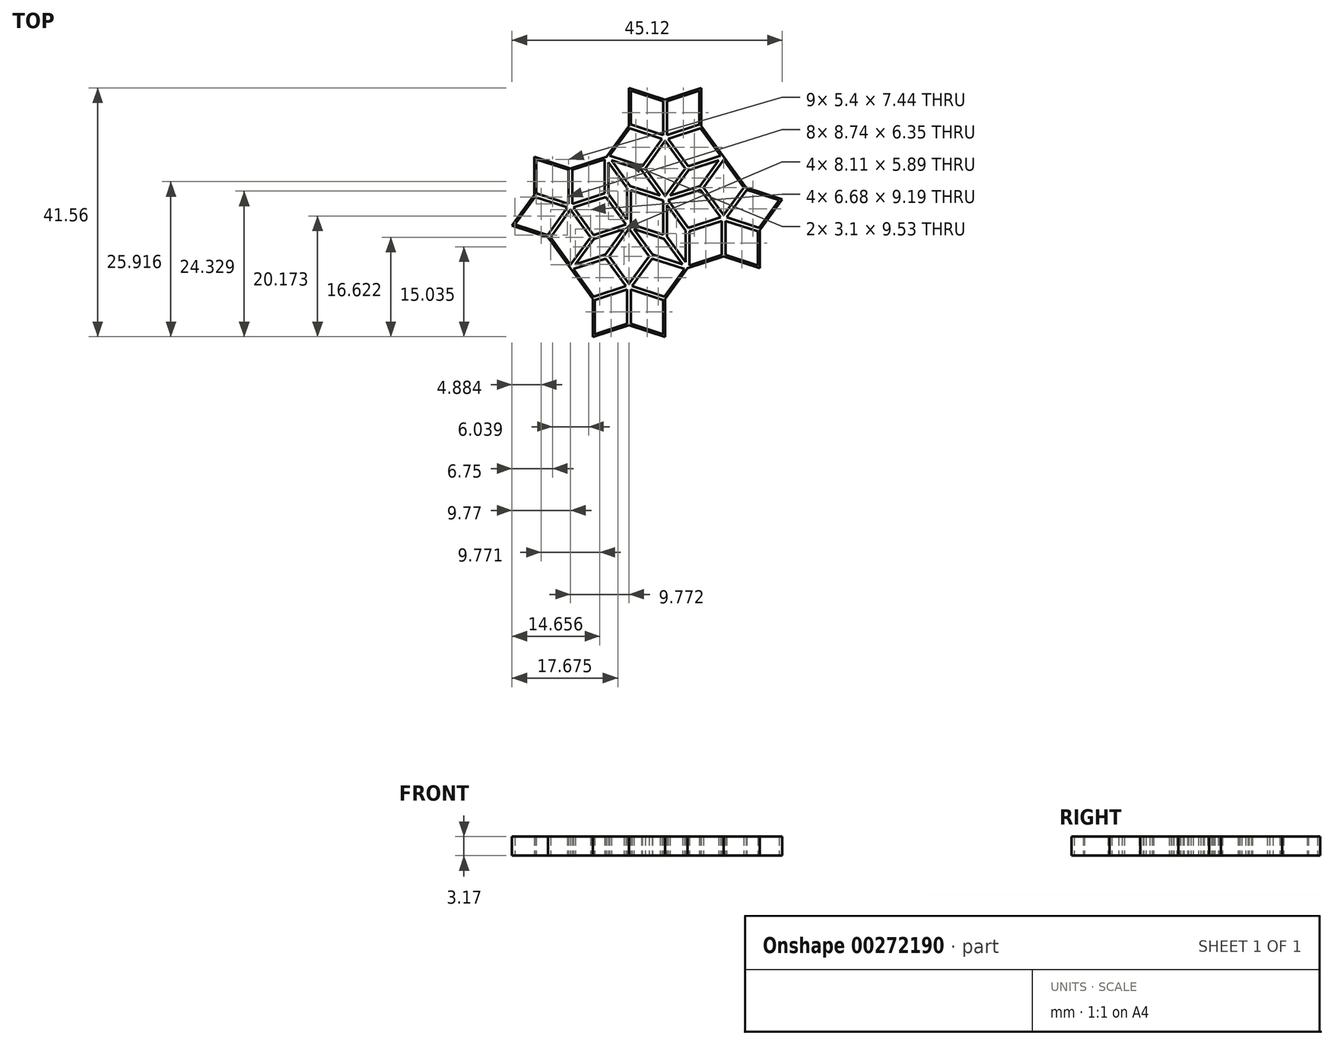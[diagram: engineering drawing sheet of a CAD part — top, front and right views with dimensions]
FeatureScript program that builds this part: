
annotation { "Feature Type Name" : "Feature", "Feature Type Description" : "" }
export const myFeature = defineFeature(function(context is Context, id is Id, definition is map)
    precondition{}
    {
        {
            var Q0;
            Q0=qCreatedBy(makeId("Top.planeOp"),FACE);
            var sketch = newSketch(context, id + "F0", { "sketchPlane" : qUnion([Q0])});
            skLineSegment(sketch, "E0", {"start": v(0, 0) * mm, "end": v(0, 6.35) * mm, "construction": true});
            skLineSegment(sketch, "E1", {"start": v(0, 6.35) * mm, "end": v(-6.04, 8.31) * mm});
            skLineSegment(sketch, "E2", {"start": v(-6.04, 8.31) * mm, "end": v(-6.04, 1.96) * mm});
            skLineSegment(sketch, "E3", {"start": v(0, 0) * mm, "end": v(-6.04, 1.96) * mm, "construction": true});
            skLineSegment(sketch, "E4.1.0", {"start": v(-6.04, 1.96) * mm, "end": v(-9.77, -3.18) * mm});
            skLineSegment(sketch, "E4.1.2", {"start": v(0, 0) * mm, "end": v(-3.73, -5.14) * mm, "construction": true});
            skLineSegment(sketch, "E4.1.3", {"start": v(-9.77, -3.17) * mm, "end": v(-3.73, -5.14) * mm});
            skLineSegment(sketch, "E4.2.0", {"start": v(-3.73, -5.14) * mm, "end": v(0, -10.27) * mm});
            skLineSegment(sketch, "E4.2.3", {"start": v(0, -10.27) * mm, "end": v(3.73, -5.14) * mm, "construction": true});
            skLineSegment(sketch, "E4.3.0", {"start": v(3.73, -5.14) * mm, "end": v(10.09, -3.07) * mm, "construction": true});
            skLineSegment(sketch, "E4.4.0", {"start": v(6.04, 1.96) * mm, "end": v(6.04, 8.31) * mm, "construction": true});
            skLineSegment(sketch, "E4.4.3", {"start": v(6.04, 8.31) * mm, "end": v(0, 6.35) * mm});
            skPoint(sketch, "E4.center", {"position": v(0, 0) * mm});
            skLineSegment(sketch, "E5", {"start": v(5.72, 2.2) * mm, "end": v(0.32, 0.44) * mm});
            skLineSegment(sketch, "E6", {"start": v(0.32, 0.43) * mm, "end": v(0.32, 6.12) * mm});
            skLineSegment(sketch, "E7.1.2", {"start": v(-0.32, 6.12) * mm, "end": v(-0.32, 0.44) * mm});
            skLineSegment(sketch, "E7.1.3", {"start": v(-0.32, 0.44) * mm, "end": v(-5.72, 2.2) * mm});
            skLineSegment(sketch, "E7.2.2", {"start": v(-5.92, 1.59) * mm, "end": v(-0.51, -0.17) * mm});
            skLineSegment(sketch, "E7.2.3", {"start": v(-0.51, -0.17) * mm, "end": v(-3.85, -4.76) * mm});
            skLineSegment(sketch, "E7.4.2", {"start": v(3.85, -4.76) * mm, "end": v(0.51, -0.17) * mm});
            skLineSegment(sketch, "E8", {"start": v(0, 0) * mm, "end": v(3.73, -5.14) * mm, "construction": true});
            skLineSegment(sketch, "E9", {"start": v(0.32, 6.12) * mm, "end": v(5.72, 7.88) * mm});
            skLineSegment(sketch, "E10", {"start": v(5.72, 7.88) * mm, "end": v(5.72, 2.2) * mm});
            skLineSegment(sketch, "E11.1.0", {"start": v(-5.72, 2.2) * mm, "end": v(-5.72, 7.88) * mm});
            skLineSegment(sketch, "E11.1.1", {"start": v(-5.72, 7.88) * mm, "end": v(-0.32, 6.12) * mm});
            skLineSegment(sketch, "E11.2.0", {"start": v(-3.85, -4.76) * mm, "end": v(-9.26, -3) * mm});
            skLineSegment(sketch, "E11.2.1", {"start": v(-9.26, -3) * mm, "end": v(-5.92, 1.59) * mm});
            skLineSegment(sketch, "E11.4.0", {"start": v(5.92, 1.59) * mm, "end": v(9.26, -3) * mm});
            skLineSegment(sketch, "E11.4.1", {"start": v(9.26, -3) * mm, "end": v(3.85, -4.76) * mm});
            skLineSegment(sketch, "E12", {"start": v(0, 0) * mm, "end": v(6.04, 1.96) * mm, "construction": true});
            skLineSegment(sketch, "E13", {"start": v(0.51, -0.17) * mm, "end": v(5.92, 1.59) * mm});
            skLineSegment(sketch, "E14.MirrorCS", {"start": v(3.34, -5.14) * mm, "end": v(0, -0.54) * mm});
            skLineSegment(sketch, "E15.MirrorCS", {"start": v(0, -0.54) * mm, "end": v(-3.34, -5.14) * mm});
            skLineSegment(sketch, "E16.MirrorCS", {"start": v(-3.34, -5.14) * mm, "end": v(0, -9.73) * mm});
            skLineSegment(sketch, "E17.MirrorCS", {"start": v(0, -9.73) * mm, "end": v(3.34, -5.14) * mm});
            skLineSegment(sketch, "E18", {"start": v(6.04, 8.31) * mm, "end": v(9.76, -3.14) * mm, "construction": true});
            skLineSegment(sketch, "E19.MirrorCS", {"start": v(9.77, 3.17) * mm, "end": v(6.04, 8.31) * mm, "construction": true});
            skLineSegment(sketch, "E20.MirrorCS", {"start": v(9.77, -3.05) * mm, "end": v(9.77, 3.18) * mm, "construction": true});
            skLineSegment(sketch, "E21.MirrorCS", {"start": v(9.77, -3.18) * mm, "end": v(6.04, 1.96) * mm, "construction": true});
            skLineSegment(sketch, "E22.MirrorCS", {"start": v(15.81, 5.14) * mm, "end": v(9.77, 3.18) * mm, "construction": true});
            skLineSegment(sketch, "E23.MirrorCS", {"start": v(6.36, 7.34) * mm, "end": v(9.45, 3.07) * mm});
            skLineSegment(sketch, "E24.MirrorCS", {"start": v(6.36, 7.34) * mm, "end": v(6.36, 2.07) * mm});
            skLineSegment(sketch, "E25.MirrorCS", {"start": v(9.45, 3.08) * mm, "end": v(9.45, -2.2) * mm});
            skLineSegment(sketch, "E26.MirrorCS", {"start": v(6.36, 2.07) * mm, "end": v(9.45, -2.2) * mm});
            skPoint(sketch, "E27.orphan", {"position": v(6.36, 7.88) * mm});
            skPoint(sketch, "E28.orphan", {"position": v(6.04, 7.77) * mm});
            skPoint(sketch, "E29.orphan", {"position": v(9.77, -3.18) * mm});
            skLineSegment(sketch, "E30", {"start": v(6.87, 7.7) * mm, "end": v(9.97, 3.45) * mm});
            skLineSegment(sketch, "E31.MirrorCS", {"start": v(6.04, 8.31) * mm, "end": v(9.77, 13.45) * mm});
            skLineSegment(sketch, "E32.MirrorCS", {"start": v(9.9, 13.08) * mm, "end": v(6.55, 8.48) * mm});
            skLineSegment(sketch, "E33.MirrorCS", {"start": v(6.55, 8.48) * mm, "end": v(11.96, 6.72) * mm});
            skLineSegment(sketch, "E34.MirrorCS", {"start": v(6.87, 7.7) * mm, "end": v(11.88, 6.08) * mm});
            skLineSegment(sketch, "E35.MirrorCS", {"start": v(9.96, 3.45) * mm, "end": v(14.98, 1.82) * mm});
            skPoint(sketch, "E36.MirrorP", {"position": v(15.81, 11.49) * mm});
            skLineSegment(sketch, "E37.MirrorCS", {"start": v(12.47, 6.35) * mm, "end": v(15.81, 1.75) * mm});
            skLineSegment(sketch, "E38.MirrorCS", {"start": v(10.09, 19.36) * mm, "end": v(10.09, 13.68) * mm});
            skLineSegment(sketch, "E39.MirrorCS", {"start": v(25.07, 8.48) * mm, "end": v(19.66, 6.72) * mm});
            skLineSegment(sketch, "E40.MirrorCS", {"start": v(21.85, 13.45) * mm, "end": v(25.58, 8.31) * mm});
            skLineSegment(sketch, "E41.MirrorCS", {"start": v(25.58, 8.31) * mm, "end": v(19.54, 6.35) * mm, "construction": true});
            skLineSegment(sketch, "E42.MirrorCS", {"start": v(11.96, 6.72) * mm, "end": v(15.3, 11.32) * mm});
            skLineSegment(sketch, "E43.MirrorCS", {"start": v(16.33, 11.32) * mm, "end": v(21.73, 13.08) * mm});
            skLineSegment(sketch, "E44.MirrorCS", {"start": v(21.53, 19.36) * mm, "end": v(16.13, 17.6) * mm});
            skLineSegment(sketch, "E45.MirrorCS", {"start": v(15.81, 1.21) * mm, "end": v(12.08, 6.35) * mm, "construction": true});
            skLineSegment(sketch, "E46.MirrorCS", {"start": v(15.5, 17.6) * mm, "end": v(10.09, 19.36) * mm});
            skLineSegment(sketch, "E47.MirrorCS", {"start": v(15.81, 1.75) * mm, "end": v(19.15, 6.35) * mm});
            skLineSegment(sketch, "E48.MirrorCS", {"start": v(21.73, 13.08) * mm, "end": v(25.07, 8.48) * mm});
            skLineSegment(sketch, "E49.MirrorCS", {"start": v(15.81, 11.49) * mm, "end": v(15.81, 17.84) * mm, "construction": true});
            skLineSegment(sketch, "E50.MirrorCS", {"start": v(15.81, 17.84) * mm, "end": v(21.85, 19.8) * mm});
            skLineSegment(sketch, "E51.MirrorCS", {"start": v(10.09, 13.68) * mm, "end": v(15.5, 11.92) * mm});
            skLineSegment(sketch, "E52.MirrorCS", {"start": v(19.66, 6.72) * mm, "end": v(16.33, 11.32) * mm});
            skLineSegment(sketch, "E53.MirrorCS", {"start": v(16.13, 17.6) * mm, "end": v(16.13, 11.92) * mm});
            skLineSegment(sketch, "E54.MirrorCS", {"start": v(15.81, 11.49) * mm, "end": v(9.77, 13.45) * mm, "construction": true});
            skLineSegment(sketch, "E55.MirrorCS", {"start": v(15.81, 11.49) * mm, "end": v(12.08, 6.35) * mm, "construction": true});
            skLineSegment(sketch, "E56.MirrorCS", {"start": v(11.88, 6.08) * mm, "end": v(14.98, 1.82) * mm});
            skLineSegment(sketch, "E57.MirrorCS", {"start": v(15.3, 11.32) * mm, "end": v(9.9, 13.08) * mm});
            skLineSegment(sketch, "E58.MirrorCS", {"start": v(15.81, 11.49) * mm, "end": v(19.54, 6.35) * mm, "construction": true});
            skLineSegment(sketch, "E59.MirrorCS", {"start": v(15.81, 10.95) * mm, "end": v(12.47, 6.35) * mm});
            skLineSegment(sketch, "E60.MirrorCS", {"start": v(16.13, 11.92) * mm, "end": v(21.53, 13.68) * mm});
            skLineSegment(sketch, "E61.MirrorCS", {"start": v(21.85, 19.8) * mm, "end": v(21.85, 13.45) * mm});
            skLineSegment(sketch, "E62.MirrorCS", {"start": v(19.15, 6.35) * mm, "end": v(15.81, 10.95) * mm});
            skLineSegment(sketch, "E63.MirrorCS", {"start": v(15.5, 11.92) * mm, "end": v(15.5, 17.6) * mm});
            skLineSegment(sketch, "E64.MirrorCS", {"start": v(21.53, 13.68) * mm, "end": v(21.53, 19.36) * mm});
            skLineSegment(sketch, "E65.MirrorCS", {"start": v(9.77, 19.8) * mm, "end": v(15.81, 17.84) * mm});
            skLineSegment(sketch, "E66.MirrorCS", {"start": v(9.77, 13.45) * mm, "end": v(9.77, 19.8) * mm});
            skLineSegment(sketch, "E67.MirrorCS", {"start": v(15.81, 11.49) * mm, "end": v(21.85, 13.45) * mm, "construction": true});
            skLineSegment(sketch, "E68.MirrorCS", {"start": v(19.54, 6.35) * mm, "end": v(15.81, 1.21) * mm, "construction": true});
            skLineSegment(sketch, "E69.MirrorCS", {"start": v(15.7, 1.25) * mm, "end": v(9.77, 3.18) * mm, "construction": true});
            skLineSegment(sketch, "E70.trimOffspring", {"start": v(10.09, 2.74) * mm, "end": v(10.09, -2.94) * mm});
            skLineSegment(sketch, "E71.trimOffspring", {"start": v(10.09, 2.74) * mm, "end": v(15.5, 0.98) * mm});
            skPoint(sketch, "E72.MirrorCS.start.orphan", {"position": v(9.58, 2.9) * mm});
            skPoint(sketch, "E73.MirrorCS.start.orphan", {"position": v(10.09, 3.28) * mm});
            skPoint(sketch, "E74.orphan", {"position": v(6.36, 8.42) * mm});
            skPoint(sketch, "E75.orphan", {"position": v(5.84, 8.04) * mm});
            skLineSegment(sketch, "E76", {"start": v(0, -10.27) * mm, "end": v(24.75, 7.7) * mm, "construction": true});
            skPoint(sketch, "E77.MirrorP", {"position": v(9.77, -13.45) * mm});
            skPoint(sketch, "E78.MirrorP", {"position": v(25.58, -1.96) * mm});
            skLineSegment(sketch, "E79.MirrorCS", {"start": v(15.5, -4.7) * mm, "end": v(15.5, 0.98) * mm});
            skLineSegment(sketch, "E80.MirrorCS", {"start": v(19.66, -3.55) * mm, "end": v(16.32, 1.05) * mm});
            skLineSegment(sketch, "E81.MirrorCS", {"start": v(19.03, -10.44) * mm, "end": v(13.63, -8.69) * mm});
            skLineSegment(sketch, "E82.MirrorCS", {"start": v(13.11, -8.31) * mm, "end": v(9.77, -3.72) * mm});
            skLineSegment(sketch, "E83.MirrorCS", {"start": v(16.13, -5.04) * mm, "end": v(16.13, 0.24) * mm});
            skPoint(sketch, "E84.MirrorP", {"position": v(15.5, -5.24) * mm});
            skPoint(sketch, "E85.MirrorP", {"position": v(16, -4.87) * mm});
            skPoint(sketch, "E86.MirrorP", {"position": v(19.23, -9.84) * mm});
            skLineSegment(sketch, "E87.MirrorCS", {"start": v(22.24, 3.17) * mm, "end": v(25.58, -1.42) * mm});
            skLineSegment(sketch, "E88.MirrorCS", {"start": v(25.58, -1.96) * mm, "end": v(21.85, 3.18) * mm, "construction": true});
            skLineSegment(sketch, "E89.MirrorCS", {"start": v(4.05, -21.32) * mm, "end": v(9.45, -19.57) * mm});
            skLineSegment(sketch, "E90.MirrorCS", {"start": v(18.71, -9.67) * mm, "end": v(15.61, -5.4) * mm});
            skLineSegment(sketch, "E91.MirrorCS", {"start": v(25.58, -1.42) * mm, "end": v(28.92, 3.17) * mm});
            skLineSegment(sketch, "E92.MirrorCS", {"start": v(4.05, -15.64) * mm, "end": v(4.05, -21.32) * mm});
            skLineSegment(sketch, "E93.MirrorCS", {"start": v(19.54, 0) * mm, "end": v(15.81, -5.14) * mm, "construction": true});
            skLineSegment(sketch, "E94.MirrorCS", {"start": v(19.86, -4.16) * mm, "end": v(25.26, -2.4) * mm});
            skLineSegment(sketch, "E95.MirrorCS", {"start": v(31.62, -3.92) * mm, "end": v(35.35, 1.21) * mm});
            skLineSegment(sketch, "E96.MirrorCS", {"start": v(9.45, -19.57) * mm, "end": v(9.45, -13.89) * mm});
            skLineSegment(sketch, "E97.MirrorCS", {"start": v(15.5, -21.32) * mm, "end": v(15.5, -15.64) * mm});
            skLineSegment(sketch, "E98.MirrorCS", {"start": v(25.58, 8.31) * mm, "end": v(21.85, 3.18) * mm, "construction": true});
            skLineSegment(sketch, "E99.MirrorCS", {"start": v(13.63, -8.69) * mm, "end": v(10.29, -13.28) * mm});
            skLineSegment(sketch, "E100.MirrorCS", {"start": v(19.54, -10.27) * mm, "end": v(15.81, -15.41) * mm});
            skLineSegment(sketch, "E101.MirrorCS", {"start": v(13.5, -8.31) * mm, "end": v(19.54, -10.27) * mm, "construction": true});
            skLineSegment(sketch, "E102.MirrorCS", {"start": v(6.04, -8.31) * mm, "end": v(9.97, -2.9) * mm, "construction": true});
            skLineSegment(sketch, "E103.MirrorCS", {"start": v(0, -10.27) * mm, "end": v(6.04, -8.31) * mm, "construction": true});
            skLineSegment(sketch, "E104.MirrorCS", {"start": v(13.7, -8.04) * mm, "end": v(10.6, -3.78) * mm});
            skLineSegment(sketch, "E105.MirrorCS", {"start": v(10.09, -13.89) * mm, "end": v(10.09, -19.57) * mm});
            skLineSegment(sketch, "E106.MirrorCS", {"start": v(21.85, 3.17) * mm, "end": v(15.81, 1.21) * mm, "construction": true});
            skLineSegment(sketch, "E107.MirrorCS", {"start": v(9.77, -13.45) * mm, "end": v(6.04, -8.31) * mm, "construction": true});
            skLineSegment(sketch, "E108.MirrorCS", {"start": v(15.81, -5.14) * mm, "end": v(19.54, -10.27) * mm, "construction": true});
            skPoint(sketch, "E109.MirrorP", {"position": v(19.03, -10.1) * mm});
            skLineSegment(sketch, "E110.MirrorCS", {"start": v(5.92, -8.69) * mm, "end": v(9.26, -13.28) * mm});
            skLineSegment(sketch, "E111.MirrorCS", {"start": v(25.58, -1.96) * mm, "end": v(19.54, -3.92) * mm, "construction": true});
            skLineSegment(sketch, "E112.MirrorCS", {"start": v(19.23, -9.3) * mm, "end": v(16.13, -5.03) * mm});
            skLineSegment(sketch, "E113.MirrorCS", {"start": v(21.73, 2.8) * mm, "end": v(25.07, -1.8) * mm});
            skLineSegment(sketch, "E114.MirrorCS", {"start": v(9.77, -13.45) * mm, "end": v(9.77, -19.8) * mm, "construction": true});
            skLineSegment(sketch, "E115.MirrorCS", {"start": v(9.89, -3.21) * mm, "end": v(15.81, -5.14) * mm, "construction": true});
            skLineSegment(sketch, "E116.MirrorCS", {"start": v(9.77, -3.18) * mm, "end": v(13.5, -8.31) * mm, "construction": true});
            skLineSegment(sketch, "E117.MirrorCS", {"start": v(25.26, -8.08) * mm, "end": v(19.86, -9.84) * mm});
            skLineSegment(sketch, "E118.MirrorCS", {"start": v(15.81, -15.41) * mm, "end": v(15.81, -21.76) * mm});
            skLineSegment(sketch, "E119.MirrorCS", {"start": v(34.84, 1.05) * mm, "end": v(31.5, -3.55) * mm});
            skLineSegment(sketch, "E120.MirrorCS", {"start": v(9.77, -13.45) * mm, "end": v(13.5, -8.31) * mm, "construction": true});
            skLineSegment(sketch, "E121.MirrorCS", {"start": v(25.58, 7.77) * mm, "end": v(22.24, 3.17) * mm});
            skLineSegment(sketch, "E122.MirrorCS", {"start": v(25.26, -2.4) * mm, "end": v(25.26, -8.08) * mm});
            skLineSegment(sketch, "E123.MirrorCS", {"start": v(19.54, -10.27) * mm, "end": v(9.8, -3.2) * mm, "construction": true});
            skLineSegment(sketch, "E124.MirrorCS", {"start": v(15.5, -4.7) * mm, "end": v(10.09, -2.94) * mm});
            skLineSegment(sketch, "E125.MirrorCS", {"start": v(18.71, -9.67) * mm, "end": v(13.7, -8.04) * mm});
            skLineSegment(sketch, "E126.MirrorCS", {"start": v(9.77, -3.72) * mm, "end": v(6.43, -8.31) * mm});
            skLineSegment(sketch, "E127.MirrorCS", {"start": v(3.73, -15.41) * mm, "end": v(0, -10.27) * mm});
            skLineSegment(sketch, "E128.MirrorCS", {"start": v(9.77, -13.45) * mm, "end": v(3.73, -15.41) * mm, "construction": true});
            skLineSegment(sketch, "E129.MirrorCS", {"start": v(25.58, -1.96) * mm, "end": v(25.58, -8.31) * mm, "construction": true});
            skLineSegment(sketch, "E130.MirrorCS", {"start": v(9.77, -12.9) * mm, "end": v(13.11, -8.31) * mm});
            skLineSegment(sketch, "E131.MirrorCS", {"start": v(26.1, -1.8) * mm, "end": v(29.44, 2.8) * mm});
            skLineSegment(sketch, "E132.MirrorCS", {"start": v(0.51, -10.44) * mm, "end": v(5.92, -8.69) * mm});
            skLineSegment(sketch, "E133.MirrorCS", {"start": v(28.92, 3.17) * mm, "end": v(25.58, 7.77) * mm});
            skLineSegment(sketch, "E134.MirrorCS", {"start": v(25.58, -1.96) * mm, "end": v(29.31, 3.17) * mm, "construction": true});
            skLineSegment(sketch, "E135.MirrorCS", {"start": v(29.44, 2.8) * mm, "end": v(34.84, 1.05) * mm});
            skLineSegment(sketch, "E136.MirrorCS", {"start": v(9.45, -13.89) * mm, "end": v(4.05, -15.64) * mm});
            skLineSegment(sketch, "E137.MirrorCS", {"start": v(15.5, -15.64) * mm, "end": v(10.09, -13.89) * mm});
            skLineSegment(sketch, "E138.MirrorCS", {"start": v(19.23, -9.3) * mm, "end": v(19.23, -4.03) * mm});
            skLineSegment(sketch, "E139.MirrorCS", {"start": v(25.07, -1.8) * mm, "end": v(19.66, -3.55) * mm});
            skLineSegment(sketch, "E140.MirrorCS", {"start": v(16.32, 1.05) * mm, "end": v(21.73, 2.8) * mm});
            skLineSegment(sketch, "E141.MirrorCS", {"start": v(6.43, -8.31) * mm, "end": v(9.77, -12.9) * mm});
            skLineSegment(sketch, "E142.MirrorCS", {"start": v(25.58, -1.96) * mm, "end": v(31.62, -3.92) * mm, "construction": true});
            skPoint(sketch, "E143.MirrorP", {"position": v(19.23, -10.38) * mm});
            skLineSegment(sketch, "E144.MirrorCS", {"start": v(15.62, -5.4) * mm, "end": v(10.6, -3.78) * mm});
            skLineSegment(sketch, "E145.MirrorCS", {"start": v(3.73, -21.76) * mm, "end": v(3.73, -15.41) * mm});
            skLineSegment(sketch, "E146.MirrorCS", {"start": v(15.69, -15.04) * mm, "end": v(19.03, -10.44) * mm});
            skLineSegment(sketch, "E147.MirrorCS", {"start": v(29.31, 3.17) * mm, "end": v(25.58, 8.31) * mm});
            skLineSegment(sketch, "E148.MirrorCS", {"start": v(31.5, -3.55) * mm, "end": v(26.1, -1.8) * mm});
            skPoint(sketch, "E149.MirrorP", {"position": v(19.74, -10) * mm});
            skLineSegment(sketch, "E150.MirrorCS", {"start": v(15.81, 1.21) * mm, "end": v(19.54, -3.92) * mm, "construction": true});
            skLineSegment(sketch, "E151.MirrorCS", {"start": v(15.81, -21.76) * mm, "end": v(9.77, -19.8) * mm});
            skLineSegment(sketch, "E152.MirrorCS", {"start": v(35.35, 1.21) * mm, "end": v(29.31, 3.17) * mm});
            skLineSegment(sketch, "E153.MirrorCS", {"start": v(19.54, -10.27) * mm, "end": v(25.58, -8.31) * mm});
            skLineSegment(sketch, "E154.MirrorCS", {"start": v(25.9, -8.08) * mm, "end": v(25.9, -2.4) * mm});
            skLineSegment(sketch, "E155.MirrorCS", {"start": v(15.81, 1.09) * mm, "end": v(15.81, -5.14) * mm, "construction": true});
            skLineSegment(sketch, "E156.MirrorCS", {"start": v(10.09, -19.57) * mm, "end": v(15.5, -21.32) * mm});
            skLineSegment(sketch, "E157.MirrorCS", {"start": v(3.85, -15.04) * mm, "end": v(0.51, -10.44) * mm});
            skLineSegment(sketch, "E158.MirrorCS", {"start": v(25.9, -2.4) * mm, "end": v(31.3, -4.16) * mm});
            skLineSegment(sketch, "E159.MirrorCS", {"start": v(9.77, -13.45) * mm, "end": v(15.81, -15.41) * mm, "construction": true});
            skLineSegment(sketch, "E160.MirrorCS", {"start": v(9.77, -19.8) * mm, "end": v(3.73, -21.76) * mm});
            skLineSegment(sketch, "E161.MirrorCS", {"start": v(9.26, -13.28) * mm, "end": v(3.85, -15.04) * mm});
            skLineSegment(sketch, "E162.MirrorCS", {"start": v(10.28, -13.28) * mm, "end": v(15.69, -15.04) * mm});
            skLineSegment(sketch, "E163.MirrorCS", {"start": v(19.86, -9.84) * mm, "end": v(19.86, -4.16) * mm});
            skLineSegment(sketch, "E164.MirrorCS", {"start": v(19.23, -4.03) * mm, "end": v(16.13, 0.24) * mm});
            skLineSegment(sketch, "E165.MirrorCS", {"start": v(25.58, -8.31) * mm, "end": v(31.62, -10.27) * mm});
            skLineSegment(sketch, "E166.MirrorCS", {"start": v(31.62, -10.27) * mm, "end": v(31.62, -3.92) * mm});
            skLineSegment(sketch, "E167.MirrorCS", {"start": v(31.3, -4.16) * mm, "end": v(31.3, -9.84) * mm});
            skLineSegment(sketch, "E168.MirrorCS", {"start": v(31.3, -9.84) * mm, "end": v(25.9, -8.08) * mm});
            skLineSegment(sketch, "E169.MirrorCS", {"start": v(8.94, -3.78) * mm, "end": v(5.84, -8.04) * mm});
            skLineSegment(sketch, "E170.MirrorCS", {"start": v(0.83, -9.67) * mm, "end": v(5.84, -8.04) * mm});
            skLineSegment(sketch, "E171.MirrorCS", {"start": v(8.94, -3.78) * mm, "end": v(3.93, -5.4) * mm});
            skLineSegment(sketch, "E172.MirrorCS", {"start": v(0.83, -9.67) * mm, "end": v(3.93, -5.4) * mm});
            skPoint(sketch, "E173.orphan", {"position": v(9.26, -3.34) * mm});
            skPoint(sketch, "E174.orphan", {"position": v(9.45, -3.61) * mm});
            skPoint(sketch, "E175.orphan", {"position": v(0.32, -9.84) * mm});
            skPoint(sketch, "E176.orphan", {"position": v(0.51, -10.1) * mm});
            skPoint(sketch, "E177.orphan", {"position": v(3.85, -5.51) * mm});
            skPoint(sketch, "E178.orphan", {"position": v(4.05, -5.37) * mm});
            skPoint(sketch, "E179.orphan", {"position": v(5.92, -7.94) * mm});
            skPoint(sketch, "E180.orphan", {"position": v(5.72, -8.08) * mm});
            skPoint(sketch, "E181.orphan", {"position": v(10.09, -3.07) * mm});
            skPoint(sketch, "E182.orphan", {"position": v(9.97, -2.9) * mm});
            skPoint(sketch, "E183.orphan", {"position": v(15.61, 0.94) * mm});
            skPoint(sketch, "E184.orphan", {"position": v(15.5, 1.1) * mm});
            skPoint(sketch, "E185.orphan", {"position": v(16.13, 1.65) * mm});
            skPoint(sketch, "E186.orphan", {"position": v(16.32, 1.38) * mm});
            skPoint(sketch, "E187.orphan", {"position": v(25.26, 7.88) * mm});
            skPoint(sketch, "E188.orphan", {"position": v(25.07, 8.15) * mm});
            skLineSegment(sketch, "E189.MirrorCS", {"start": v(16.64, 1.82) * mm, "end": v(19.74, 6.08) * mm});
            skLineSegment(sketch, "E190.MirrorCS", {"start": v(16.64, 1.82) * mm, "end": v(21.65, 3.45) * mm});
            skLineSegment(sketch, "E191.MirrorCS", {"start": v(24.75, 7.7) * mm, "end": v(19.74, 6.08) * mm});
            skLineSegment(sketch, "E192.MirrorCS", {"start": v(24.75, 7.7) * mm, "end": v(21.65, 3.45) * mm});
            skSolve(sketch);
        }
        {
            var Q0;
            Q0=makeQuery(id+"F0.imprint","IMPRINT",FACE,{"disambiguationData":[TD([[makeQuery(id+"F0.imprint","IMPRINT",EDGE,{"derivedFrom":sQuery(id+"F0.wireOp",EDGE,"E1")}),1.0]])]});
            var Q1;
            Q1=makeQuery(id+"F0.imprint","IMPRINT",FACE,{"disambiguationData":[TD([[makeQuery(id+"F0.imprint","IMPRINT",EDGE,{"derivedFrom":sQuery(id+"F0.wireOp",EDGE,"df5f55fc-6b28-459b-9301-4e840687e23f2.MirrorCS")}),-1.0]])]});
            extrude(context, id + "F1", {"entities" : qUnion([Q0, Q1]), "depth" : 3.17 * mm});
        }
    });
